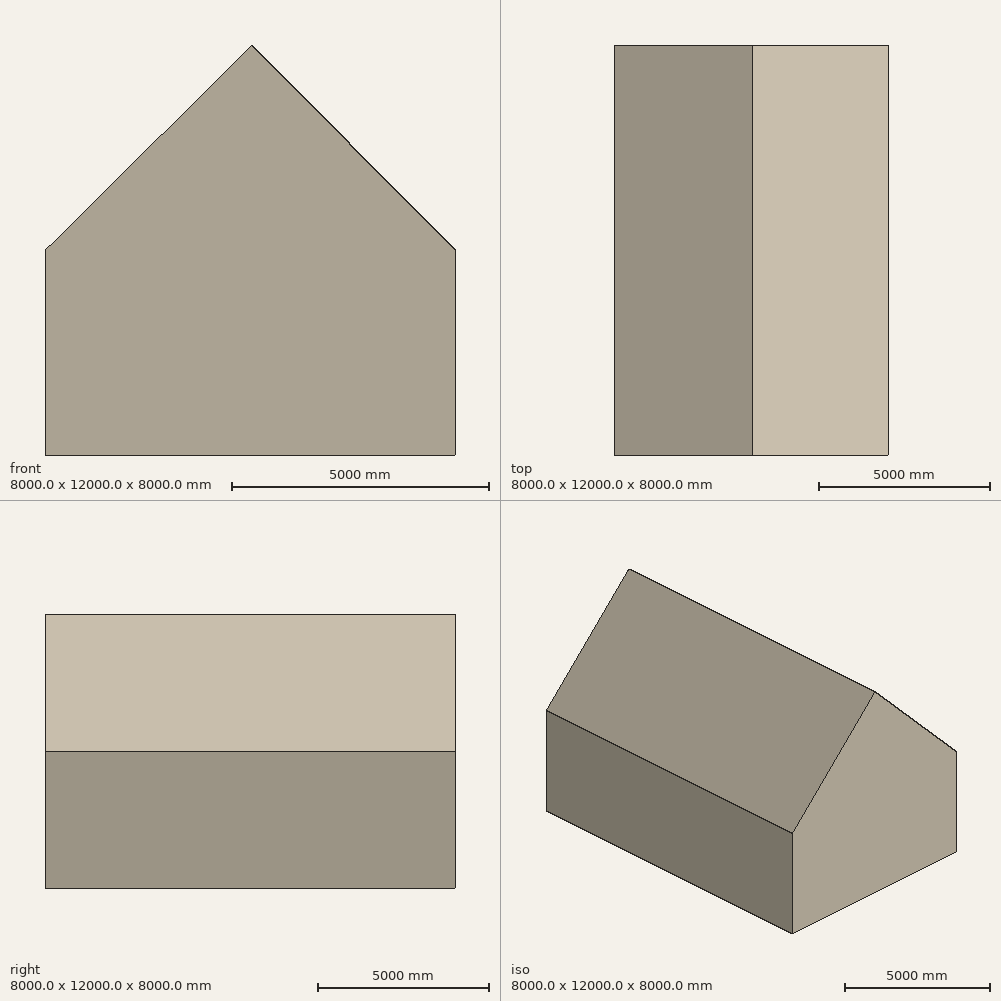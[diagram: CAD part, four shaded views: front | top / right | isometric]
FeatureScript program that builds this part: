
annotation { "Feature Type Name" : "Feature", "Feature Type Description" : "" }
export const myFeature = defineFeature(function(context is Context, id is Id, definition is map)
    precondition{}
    {
        {
            var Q0;
            Q0=qCreatedBy(makeId("Front.planeOp"),FACE);
            var sketch = newSketch(context, id + "F0", { "sketchPlane" : qUnion([Q0])});
            skLineSegment(sketch, "E0", {"start": v(-4035.82, 4000) * mm, "end": v(-4035.82, 0) * mm});
            skLineSegment(sketch, "E1", {"start": v(-4035.82, 0) * mm, "end": v(3964.18, 0) * mm});
            skLineSegment(sketch, "E2", {"start": v(3964.18, 0) * mm, "end": v(3964.18, 4000) * mm});
            skLineSegment(sketch, "E3", {"start": v(0, 0) * mm, "end": v(0, 8000) * mm});
            skLineSegment(sketch, "E4", {"start": v(0, 8000) * mm, "end": v(-4035.82, 4000) * mm});
            skLineSegment(sketch, "E5", {"start": v(0, 8000) * mm, "end": v(3964.18, 4000) * mm});
            skSolve(sketch);
        }
        {
            var Q0;
            {var subQ0=sQuery(id+"F0.wireOp",EDGE,"E0");Q0=makeQuery(id+"F0.imprint","IMPRINT",FACE,{"disambiguationData":[TD([[makeQuery(id+"F0.imprint","IMPRINT",EDGE,{"derivedFrom":subQ0}),1.0]])]});}
            var Q1;
            {var subQ0=sQuery(id+"F0.wireOp",EDGE,"E2");Q1=makeQuery(id+"F0.imprint","IMPRINT",FACE,{"disambiguationData":[TD([[makeQuery(id+"F0.imprint","IMPRINT",EDGE,{"derivedFrom":subQ0}),1.0]])]});}
            extrude(context, id + "F1", {"entities" : qUnion([Q0, Q1]), "depth" : 12000 * mm});
        }
    });
